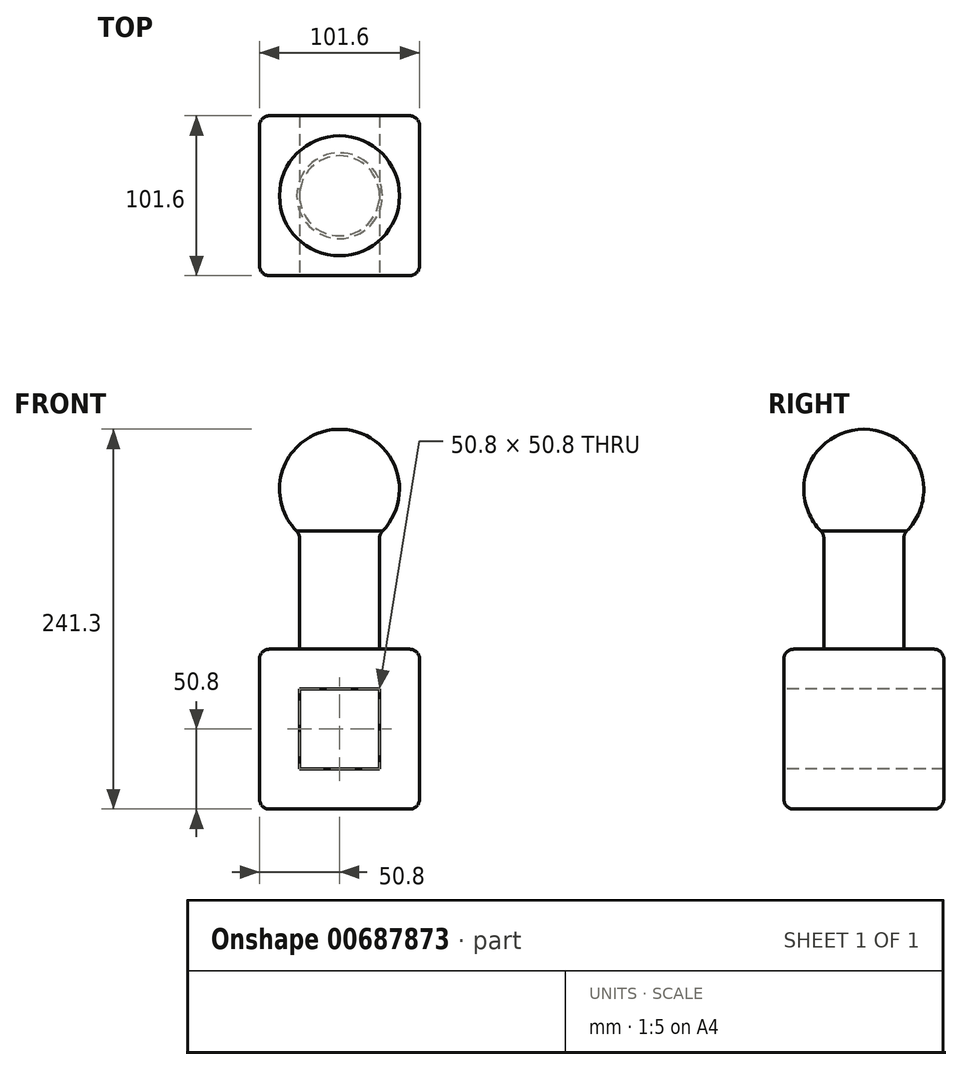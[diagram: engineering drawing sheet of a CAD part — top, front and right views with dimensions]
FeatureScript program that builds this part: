
annotation { "Feature Type Name" : "Feature", "Feature Type Description" : "" }
export const myFeature = defineFeature(function(context is Context, id is Id, definition is map)
    precondition{}
    {
        {
            var Q0;
            Q0=qCreatedBy(makeId("Top.planeOp"),FACE);
            var sketch = newSketch(context, id + "F0", { "sketchPlane" : qUnion([Q0])});
            skLineSegment(sketch, "E0.bottom", {"start": v(50.8, -50.8) * mm, "end": v(-50.8, -50.8) * mm});
            skLineSegment(sketch, "E0.top", {"start": v(50.8, 50.8) * mm, "end": v(-50.8, 50.8) * mm});
            skLineSegment(sketch, "E0.left", {"start": v(50.8, -50.8) * mm, "end": v(50.8, 50.8) * mm});
            skLineSegment(sketch, "E0.right", {"start": v(-50.8, -50.8) * mm, "end": v(-50.8, 50.8) * mm});
            skPoint(sketch, "E0.middle", {"position": v(0, 0) * mm});
            skSolve(sketch);
        }
        {
            var Q0;
            Q0 = qSketchRegion(id + "F0", true);
            extrude(context, id + "F1", {"entities" : qUnion([Q0]), "depth" : 101.6 * mm, "offsetDistance" : 25.4 * mm});
        }
        {
            var Q0;
            Q0=makeQuery(id+"F1.opExtrude","CAP_FACE",FACE,{"disambiguationData":[OSD([sQuery(id+"F0.wireOp",EDGE,"E0.bottom"),sQuery(id+"F0.wireOp",EDGE,"E0.top"),sQuery(id+"F0.wireOp",EDGE,"E0.left"),sQuery(id+"F0.wireOp",EDGE,"E0.right")])],"isStart":false});
            var sketch = newSketch(context, id + "F2", { "sketchPlane" : qUnion([Q0])});
            skCircle(sketch, "E1", {"center": v(0, 0) * mm, "radius": 25.4 * mm});
            skSolve(sketch);
        }
        {
            var Q0;
            Q0=makeQuery(id+"F2.imprint","IMPRINT",FACE,{"disambiguationData":[TD([[makeQuery(id+"F2.imprint","IMPRINT",EDGE,{"derivedFrom":sQuery(id+"F2.wireOp",EDGE,"E1")}),1.0]])]});
            extrude(context, id + "F3", {"entities" : qUnion([Q0]), "operationType" : NewBodyOperationType.ADD, "depth" : 101.6 * mm, "offsetDistance" : 25.4 * mm});
        }
        {
            var Q0;
            Q0=makeQuery(id+"F3.opExtrude","CAP_FACE",FACE,{"disambiguationData":[OSD([sQuery(id+"F2.wireOp",EDGE,"E1")])],"isStart":false});
            var sketch = newSketch(context, id + "F4", { "sketchPlane" : qUnion([Q0])});
            skArc(sketch, "E2", {"start": v(0, -38.1) * mm, "mid": v(38.1, 0) * mm, "end": v(0, 38.1) * mm});
            skLineSegment(sketch, "E3", {"start": v(0, 38.1) * mm, "end": v(0, -38.1) * mm});
            skSolve(sketch);
        }
        {
            var Q0;
            {var subQ0=sQuery(id+"F4.wireOp",EDGE,"E2");Q0=makeQuery(id+"F4.imprint","IMPRINT",FACE,{"disambiguationData":[TD([[makeQuery(id+"F4.imprint","IMPRINT",EDGE,{"derivedFrom":subQ0}),1.0]])]});}
            var Q1;
            {var subQ0=sQuery(id+"F4.wireOp",EDGE,"E3");var subQ1=makeQuery(id+"F3.opExtrude","CAP_EDGE",EDGE,{"disambiguationData":[OSD([sQuery(id+"F2.wireOp",EDGE,"E1")])],"isStart":false});var subQ2=makeQuery(id+"F4.imprint","INTERSECT",VERTEX,{"disambiguationData":[OD(0.0)],"derivedFrom":[subQ1,subQ0]});Q1=makeQuery(id+"F4.imprint","IMPRINT",FACE,{"disambiguationData":[TD([[makeQuery(id+"F4.imprint","IMPRINT",EDGE,{"disambiguationData":[TD([[subQ2,-1.0]])],"derivedFrom":subQ0}),1.0]])]});}
            var Q2;
            Q2=sQuery(id+"F4.wireOp",EDGE,"E3");
            revolve(context, id + "F5", {"operationType" : NewBodyOperationType.ADD, "entities" : qUnion([Q0, Q1]), "axis" : qUnion([Q2]), "revolveType" : RevolveType.FULL});
        }
        {
            var Q0;
            Q0=makeQuery(id+"F1.opExtrude","SWEPT_FACE",FACE,{"disambiguationData":[OSD([sQuery(id+"F0.wireOp",EDGE,"E0.bottom")])]});
            var sketch = newSketch(context, id + "F6", { "sketchPlane" : qUnion([Q0])});
            skLineSegment(sketch, "E4.bottom", {"start": v(25.4, 25.4) * mm, "end": v(-25.4, 25.4) * mm});
            skLineSegment(sketch, "E4.top", {"start": v(25.4, 76.2) * mm, "end": v(-25.4, 76.2) * mm});
            skLineSegment(sketch, "E4.left", {"start": v(25.4, 25.4) * mm, "end": v(25.4, 76.2) * mm});
            skLineSegment(sketch, "E4.right", {"start": v(-25.4, 25.4) * mm, "end": v(-25.4, 76.2) * mm});
            skPoint(sketch, "E4.middle", {"position": v(0, 50.8) * mm});
            skPoint(sketch, "E4.middle.positionSnap0", {"position": v(50.8, 50.8) * mm});
            skPoint(sketch, "E4.middle.positionSnap1", {"position": v(0, 0) * mm});
            skPoint(sketch, "E4.centerSnap0", {"position": v(50.8, 50.8) * mm});
            skPoint(sketch, "E4.centerSnap1", {"position": v(0, 0) * mm});
            skSolve(sketch);
        }
        {
            var Q0;
            Q0=makeQuery(id+"F6.imprint","IMPRINT",FACE,{"disambiguationData":[TD([[makeQuery(id+"F6.imprint","IMPRINT",EDGE,{"derivedFrom":sQuery(id+"F6.wireOp",EDGE,"E4.bottom")}),-1.0]])]});
            extrude(context, id + "F7", {"entities" : qUnion([Q0]), "operationType" : NewBodyOperationType.REMOVE, "oppositeDirection" : true, "depth" : 101.6 * mm, "offsetDistance" : 25.4 * mm});
        }
        {
            var Q0;
            Q0=makeQuery(id+"F1.opExtrude","CAP_EDGE",EDGE,{"disambiguationData":[OSD([sQuery(id+"F0.wireOp",EDGE,"E0.left")])],"isStart":false});
            var Q1;
            Q1=makeQuery(id+"F1.opExtrude","SWEPT_EDGE",EDGE,{"disambiguationData":[OSD([sQuery(id+"F0.wireOp",EDGE,"E0.top"),sQuery(id+"F0.wireOp",EDGE,"E0.left")])]});
            var Q2;
            Q2=makeQuery(id+"F1.opExtrude","SWEPT_EDGE",EDGE,{"disambiguationData":[OSD([sQuery(id+"F0.wireOp",EDGE,"E0.bottom"),sQuery(id+"F0.wireOp",EDGE,"E0.left")])]});
            var Q3;
            Q3=makeQuery(id+"F1.opExtrude","CAP_EDGE",EDGE,{"disambiguationData":[OSD([sQuery(id+"F0.wireOp",EDGE,"E0.left")])],"isStart":true});
            var Q4;
            Q4=makeQuery(id+"F1.opExtrude","CAP_EDGE",EDGE,{"disambiguationData":[OSD([sQuery(id+"F0.wireOp",EDGE,"E0.right")])],"isStart":false});
            var Q5;
            Q5=makeQuery(id+"F1.opExtrude","CAP_EDGE",EDGE,{"disambiguationData":[OSD([sQuery(id+"F0.wireOp",EDGE,"E0.bottom")])],"isStart":false});
            var Q6;
            Q6=makeQuery(id+"F1.opExtrude","SWEPT_EDGE",EDGE,{"disambiguationData":[OSD([sQuery(id+"F0.wireOp",EDGE,"E0.bottom"),sQuery(id+"F0.wireOp",EDGE,"E0.right")])]});
            var Q7;
            Q7=makeQuery(id+"F1.opExtrude","CAP_EDGE",EDGE,{"disambiguationData":[OSD([sQuery(id+"F0.wireOp",EDGE,"E0.top")])],"isStart":false});
            var Q8;
            Q8=makeQuery(id+"F1.opExtrude","CAP_EDGE",EDGE,{"disambiguationData":[OSD([sQuery(id+"F0.wireOp",EDGE,"E0.bottom")])],"isStart":true});
            var Q9;
            Q9=makeQuery(id+"F1.opExtrude","SWEPT_EDGE",EDGE,{"disambiguationData":[OSD([sQuery(id+"F0.wireOp",EDGE,"E0.top"),sQuery(id+"F0.wireOp",EDGE,"E0.right")])]});
            var Q10;
            Q10=makeQuery(id+"F1.opExtrude","CAP_EDGE",EDGE,{"disambiguationData":[OSD([sQuery(id+"F0.wireOp",EDGE,"E0.top")])],"isStart":true});
            var Q11;
            Q11=makeQuery(id+"F1.opExtrude","CAP_EDGE",EDGE,{"disambiguationData":[OSD([sQuery(id+"F0.wireOp",EDGE,"E0.right")])],"isStart":true});
            var Q12;
            Q12=makeQuery(id+"F3.opExtrude","CAP_EDGE",EDGE,{"disambiguationData":[OSD([sQuery(id+"F2.wireOp",EDGE,"E1")])],"isStart":true});
            var Q13;
            Q13=makeQuery(id+"F5.boolean.opBoolean","INTERSECT",EDGE,{"derivedFrom":[makeQuery(id+"F3.opExtrude","SWEPT_FACE",FACE,{"disambiguationData":[OSD([sQuery(id+"F2.wireOp",EDGE,"E1")])]}),makeQuery(id+"F5.opRevolve","SWEPT_FACE",FACE,{"disambiguationData":[OSD([sQuery(id+"F4.wireOp",EDGE,"E2")])]})]});
            fillet(context, id + "F8", {"entities" : qUnion([Q0, Q1, Q2, Q3, Q4, Q5, Q6, Q7, Q8, Q9, Q10, Q11, Q12, Q13]), "radius" : 6.35 * mm, "tangentPropagation" : true, "allowEdgeOverflow" : false});
        }
    });
